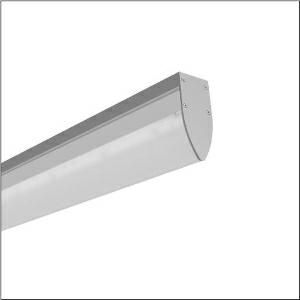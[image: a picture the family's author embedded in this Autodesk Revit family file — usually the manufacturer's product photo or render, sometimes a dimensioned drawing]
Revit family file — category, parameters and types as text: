
# Revit family: mira_21_td_51fr527g434a
name_source: partatom
category: Lighting Fixtures
units: mm (PartAtom-declared; Revit-internal decimal feet)

## family parameters
Cut with Voids When Loaded = No
Host = Face
Light Source = No
Part Type = Normal
Room Calculation Point = No
Round Connector Dimension = Use Diameter
Shared = No

## types (1)
- Mira 21 TD (1 x LED, 3020 lm, 20 W, 4000K)
    Apparent Load = 20 VA
    CIE Flux Codes = 40 68 87 81 100
    Color Rendering = 80
    Color Temperature = 4000K
    Default Elevation = 1800 mm
    Description = Mira 21 TD, clean room luminaire, primary light control with reflector, primary optical cover: cover, of PMMA, frosted, light emission: direct distribution, primary light characteristic: symmetric, installation type: surface-mounted, LED, rated luminous flux: 3.020lm, luminous efficacy: 151lm/W, light colour: 840, colour temperature: 4000K, control gear: ON/OFF, with terminal, 3-pole, max. 2.5mm², mains connection: 230V, AC, 50/60Hz, rated input power: 20W, luminaire housing, of sheet steel, coated, pure white (RAL 9010), length: 900mm, width: 55mm, height: 120mm, protection rating (complete): IP43, insulation class (complete): insulation class I (protective earthing), certification: CE, UKCA, permissible operating ambient temperature: -5..+40°C, standard: EN 50419, packaging unit: 1 piece
    Height = 120 mm
    Lamp = 1 x LED
    Lamp Light Flux = 3020 lm
    Lamp Power = 20 W
    Lamp count = 1
    Length = 900 mm
    Luminous efficacy = 151 lm/W
    Manufacturer = Siteco
    ModVariant = No
    Model = 51FR527G434A
    Mounting Place = Ceiling
    Mounting Type = Surface mounted
    Number of Poles = 1
    OnlyDefault = Yes
    Power Factor = 1
    Product Name = Mira 21 TD
    Product group = clean room luminaire | ceiling mounted
    ProductGroupID = 306
    Protection Class = Protection class I
    Protection Degree = IP 43
    RLX_Detail_Level = 1
    RLX_Emergency_Light_Flux = 0 lm
    RLX_Emergency_Type = 0
    RLX_Emergency_Type_DB = No
    RlxData = <blob elided: 25141 chars, md5=8acc7a4a>
    Socket = socket
    Standby Power = 0 W
    System Light Flux = 3020 lm
    System Power = 20 W
    Type Comments = Product without accessories
    Type Image = l_1007115.jpg
    URL = http://relux.com
    VarID = ---
    Voltage = 0 V
    Weight = 0.00 kg
    Width = 55 mm

## geometry (parser evidence)
native form markers: Blend x4, Sweep x13
no freeform markers — native parametric forms only
